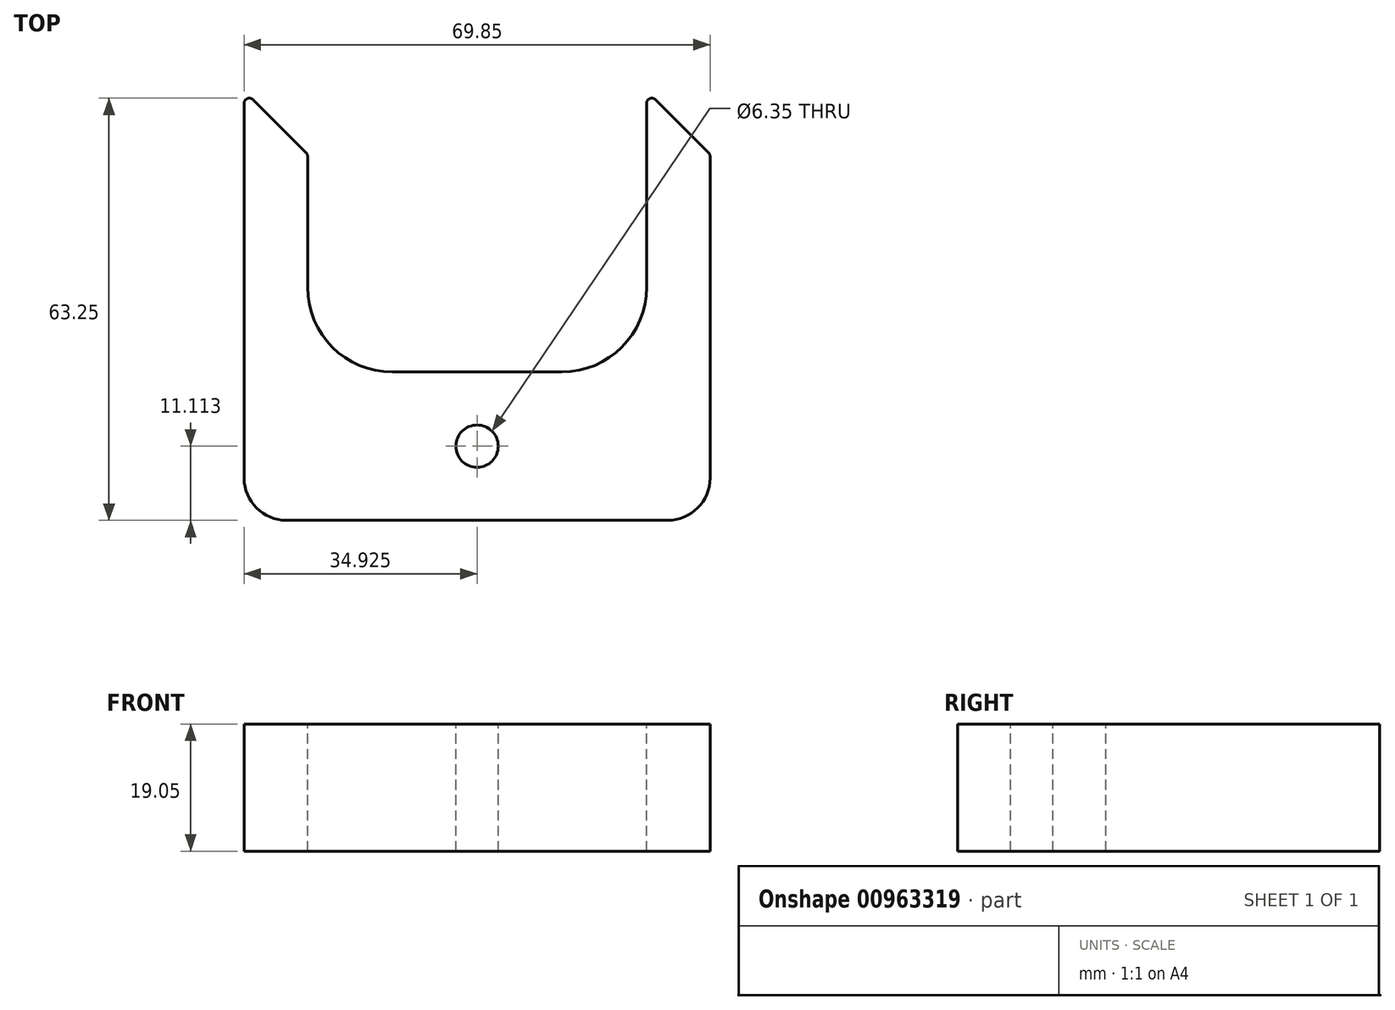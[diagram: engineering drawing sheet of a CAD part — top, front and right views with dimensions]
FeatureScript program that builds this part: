
annotation { "Feature Type Name" : "Feature", "Feature Type Description" : "" }
export const myFeature = defineFeature(function(context is Context, id is Id, definition is map)
    precondition{}
    {
        {
            var Q0;
            Q0=qCreatedBy(makeId("Top.planeOp"),FACE);
            var sketch = newSketch(context, id + "F0", { "sketchPlane" : qUnion([Q0])});
            skLineSegment(sketch, "E0.bottom", {"start": v(6.35, 0) * mm, "end": v(63.5, 0) * mm});
            skLineSegment(sketch, "E0.top", {"start": v(6.35, 120.65) * mm, "end": v(63.5, 120.65) * mm});
            skLineSegment(sketch, "E0.left", {"start": v(0, 6.35) * mm, "end": v(0, 114.3) * mm});
            skLineSegment(sketch, "E0.right", {"start": v(69.85, 6.35) * mm, "end": v(69.85, 114.3) * mm});
            skPoint(sketch, "E1.visualSharp", {"position": v(69.85, 0) * mm});
            skArc(sketch, "E1.filletArc", {"start": v(63.5, 0) * mm, "mid": v(68, 1.86) * mm, "end": v(69.85, 6.35) * mm});
            skPoint(sketch, "E2.visualSharp", {"position": v(0, 0) * mm});
            skArc(sketch, "E2.filletArc", {"start": v(0, 6.35) * mm, "mid": v(1.86, 1.86) * mm, "end": v(6.35, 0) * mm});
            skPoint(sketch, "E3.visualSharp", {"position": v(0, 120.65) * mm});
            skArc(sketch, "E3.filletArc", {"start": v(6.35, 120.65) * mm, "mid": v(1.86, 118.8) * mm, "end": v(0, 114.3) * mm});
            skPoint(sketch, "E4.visualSharp", {"position": v(69.85, 120.65) * mm});
            skArc(sketch, "E4.filletArc", {"start": v(69.85, 114.3) * mm, "mid": v(68, 118.8) * mm, "end": v(63.5, 120.65) * mm});
            skSolve(sketch);
        }
        {
            var Q0;
            Q0 = qSketchRegion(id + "F0", true);
            extrude(context, id + "F1", {"entities" : qUnion([Q0]), "depth" : 19.05 * mm, "offsetDistance" : 25.4 * mm});
        }
        {
            var Q0;
            Q0=makeQuery(id+"F1.opExtrude","CAP_FACE",FACE,{"disambiguationData":[OSD([sQuery(id+"F0.wireOp",EDGE,"E0.bottom"),sQuery(id+"F0.wireOp",EDGE,"E0.top"),sQuery(id+"F0.wireOp",EDGE,"E0.left"),sQuery(id+"F0.wireOp",EDGE,"E0.right"),sQuery(id+"F0.wireOp",EDGE,"E1.filletArc"),sQuery(id+"F0.wireOp",EDGE,"E2.filletArc"),sQuery(id+"F0.wireOp",EDGE,"E3.filletArc"),sQuery(id+"F0.wireOp",EDGE,"E4.filletArc")])],"isStart":false});
            var sketch = newSketch(context, id + "F2", { "sketchPlane" : qUnion([Q0])});
            skCircle(sketch, "E5", {"center": v(34.92, 109.54) * mm, "radius": 3.18 * mm});
            skCircle(sketch, "E6", {"center": v(34.92, 11.11) * mm, "radius": 3.18 * mm});
            skLineSegment(sketch, "E7", {"start": v(34.92, 120.65) * mm, "end": v(34.92, 109.54) * mm, "construction": true});
            skLineSegment(sketch, "E8", {"start": v(34.92, 109.54) * mm, "end": v(34.92, 11.11) * mm, "construction": true});
            skLineSegment(sketch, "E9", {"start": v(34.92, 11.11) * mm, "end": v(34.93, 0) * mm, "construction": true});
            skLineSegment(sketch, "E10.bottom", {"start": v(22.22, 98.43) * mm, "end": v(47.62, 98.43) * mm});
            skLineSegment(sketch, "E10.top", {"start": v(22.22, 22.23) * mm, "end": v(47.62, 22.23) * mm});
            skLineSegment(sketch, "E10.left", {"start": v(9.52, 85.73) * mm, "end": v(9.52, 34.93) * mm});
            skLineSegment(sketch, "E10.right", {"start": v(60.32, 85.73) * mm, "end": v(60.32, 34.93) * mm});
            skPoint(sketch, "E11.visualSharp", {"position": v(9.52, 98.43) * mm});
            skArc(sketch, "E11.filletArc", {"start": v(22.22, 98.43) * mm, "mid": v(13.24, 94.7) * mm, "end": v(9.52, 85.73) * mm});
            skPoint(sketch, "E12.visualSharp", {"position": v(60.32, 98.43) * mm});
            skArc(sketch, "E12.filletArc", {"start": v(60.32, 85.73) * mm, "mid": v(56.6, 94.7) * mm, "end": v(47.62, 98.43) * mm});
            skPoint(sketch, "E13.visualSharp", {"position": v(60.32, 22.23) * mm});
            skArc(sketch, "E13.filletArc", {"start": v(47.62, 22.23) * mm, "mid": v(56.6, 25.94) * mm, "end": v(60.32, 34.93) * mm});
            skPoint(sketch, "E14.visualSharp", {"position": v(9.52, 22.23) * mm});
            skArc(sketch, "E14.filletArc", {"start": v(9.52, 34.93) * mm, "mid": v(13.24, 25.94) * mm, "end": v(22.22, 22.23) * mm});
            skSolve(sketch);
        }
        {
            var Q0;
            Q0 = qSketchRegion(id + "F2", true);
            extrude(context, id + "F3", {"entities" : qUnion([Q0]), "operationType" : NewBodyOperationType.REMOVE, "endBound" : BoundingType.THROUGH_ALL, "oppositeDirection" : true, "depth" : 25.4 * mm, "offsetDistance" : 25.4 * mm});
        }
        {
            var Q0;
            Q0=makeQuery(id+"F1.opExtrude","CAP_FACE",FACE,{"disambiguationData":[OSD([sQuery(id+"F0.wireOp",EDGE,"E0.bottom"),sQuery(id+"F0.wireOp",EDGE,"E0.top"),sQuery(id+"F0.wireOp",EDGE,"E0.left"),sQuery(id+"F0.wireOp",EDGE,"E0.right"),sQuery(id+"F0.wireOp",EDGE,"E1.filletArc"),sQuery(id+"F0.wireOp",EDGE,"E2.filletArc"),sQuery(id+"F0.wireOp",EDGE,"E3.filletArc"),sQuery(id+"F0.wireOp",EDGE,"E4.filletArc")])],"isStart":false});
            var sketch = newSketch(context, id + "F4", { "sketchPlane" : qUnion([Q0])});
            skLineSegment(sketch, "E15", {"start": v(0, 60.33) * mm, "end": v(9.52, 60.33) * mm, "construction": true});
            skLineSegment(sketch, "E16", {"start": v(60.32, 60.33) * mm, "end": v(69.85, 60.33) * mm, "construction": true});
            skPoint(sketch, "E17", {"position": v(4.76, 60.33) * mm});
            skPoint(sketch, "E18", {"position": v(65.09, 60.33) * mm});
            skLineSegment(sketch, "E19", {"start": v(0, 65.09) * mm, "end": v(9.52, 55.56) * mm, "construction": true});
            skLineSegment(sketch, "E20.0", {"start": v(1.36, 63.01) * mm, "end": v(9.3, 55.08) * mm});
            skLineSegment(sketch, "E21", {"start": v(60.33, 65.09) * mm, "end": v(69.85, 55.56) * mm, "construction": true});
            skLineSegment(sketch, "E22.0", {"start": v(61.68, 63.01) * mm, "end": v(69.62, 55.08) * mm});
            skPoint(sketch, "E23.visualSharp", {"position": v(9.52, 54.84) * mm});
            skArc(sketch, "E23.filletArc", {"start": v(9.52, 54.52) * mm, "mid": v(9.46, 54.82) * mm, "end": v(9.3, 55.08) * mm});
            skPoint(sketch, "E24.visualSharp", {"position": v(0, 64.37) * mm});
            skArc(sketch, "E24.filletArc", {"start": v(1.36, 63.01) * mm, "mid": v(0.49, 63.19) * mm, "end": v(0, 62.45) * mm});
            skPoint(sketch, "E25.visualSharp", {"position": v(60.32, 64.37) * mm});
            skArc(sketch, "E25.filletArc", {"start": v(61.68, 63.01) * mm, "mid": v(60.81, 63.19) * mm, "end": v(60.32, 62.45) * mm});
            skPoint(sketch, "E26.visualSharp", {"position": v(69.85, 54.84) * mm});
            skArc(sketch, "E26.filletArc", {"start": v(69.85, 54.52) * mm, "mid": v(69.79, 54.82) * mm, "end": v(69.62, 55.08) * mm});
            skLineSegment(sketch, "E27.0", {"start": v(0, 62.45) * mm, "end": v(0, 114.3) * mm});
            skArc(sketch, "E27.1", {"start": v(6.35, 120.65) * mm, "mid": v(1.86, 118.8) * mm, "end": v(0, 114.3) * mm});
            skLineSegment(sketch, "E27.2", {"start": v(6.35, 120.65) * mm, "end": v(63.5, 120.65) * mm});
            skArc(sketch, "E27.3", {"start": v(69.85, 114.3) * mm, "mid": v(68, 118.8) * mm, "end": v(63.5, 120.65) * mm});
            skLineSegment(sketch, "E27.4", {"start": v(69.85, 54.52) * mm, "end": v(69.85, 114.3) * mm});
            skLineSegment(sketch, "E27.5", {"start": v(60.32, 85.73) * mm, "end": v(60.32, 62.45) * mm});
            skArc(sketch, "E27.6", {"start": v(60.33, 85.73) * mm, "mid": v(56.6, 94.7) * mm, "end": v(47.62, 98.43) * mm});
            skLineSegment(sketch, "E27.7", {"start": v(22.22, 98.43) * mm, "end": v(47.62, 98.43) * mm});
            skArc(sketch, "E27.8", {"start": v(22.22, 98.43) * mm, "mid": v(13.24, 94.7) * mm, "end": v(9.52, 85.73) * mm});
            skLineSegment(sketch, "E27.9", {"start": v(9.52, 85.73) * mm, "end": v(9.52, 54.52) * mm});
            skPoint(sketch, "E28.orphan", {"position": v(0, 6.35) * mm});
            skPoint(sketch, "E29.orphan", {"position": v(9.52, 34.93) * mm});
            skPoint(sketch, "E30.orphan", {"position": v(69.85, 6.35) * mm});
            skPoint(sketch, "E31.orphan", {"position": v(60.32, 34.93) * mm});
            skSolve(sketch);
        }
        {
            var Q0;
            Q0 = qSketchRegion(id + "F4", true);
            extrude(context, id + "F5", {"entities" : qUnion([Q0]), "operationType" : NewBodyOperationType.REMOVE, "endBound" : BoundingType.THROUGH_ALL, "oppositeDirection" : true, "depth" : 25.4 * mm, "offsetDistance" : 25.4 * mm});
        }
    });
